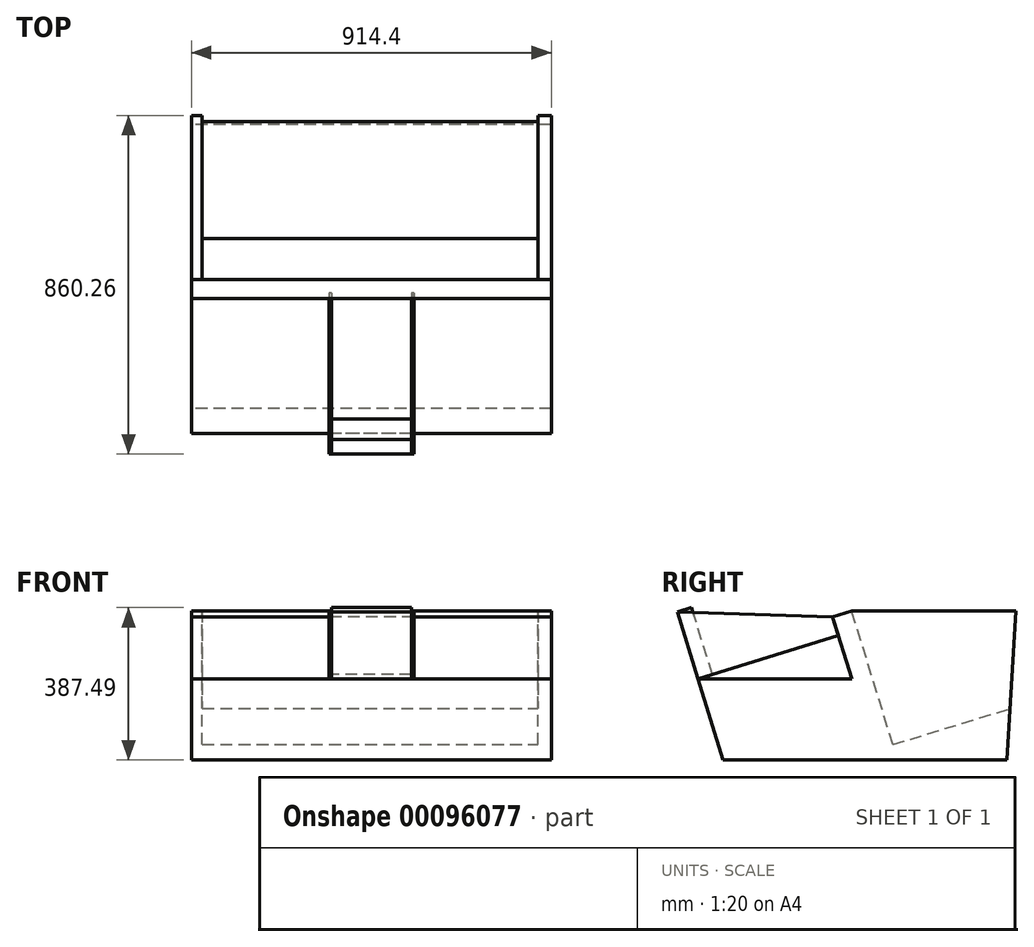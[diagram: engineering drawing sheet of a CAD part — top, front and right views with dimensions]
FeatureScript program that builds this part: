
annotation { "Feature Type Name" : "Feature", "Feature Type Description" : "" }
export const myFeature = defineFeature(function(context is Context, id is Id, definition is map)
    precondition{}
    {
        {
            var Q0;
            Q0=qCreatedBy(makeId("Right.planeOp"),FACE);
            var sketch = newSketch(context, id + "F0", { "sketchPlane" : qUnion([Q0])});
            skLineSegment(sketch, "E0", {"start": v(-51.02, 165.8) * mm, "end": v(61.03, -198.34) * mm});
            skLineSegment(sketch, "E1", {"start": v(-2.47, 8.01) * mm, "end": v(-393.28, 8.01) * mm});
            skLineSegment(sketch, "E2", {"start": v(-393.28, 8.01) * mm, "end": v(-329.78, -198.34) * mm});
            skLineSegment(sketch, "E3", {"start": v(-329.78, -198.34) * mm, "end": v(391.76, -198.34) * mm});
            skLineSegment(sketch, "E4", {"start": v(-51.02, 165.8) * mm, "end": v(-2.47, 180.75) * mm});
            skLineSegment(sketch, "E5", {"start": v(-2.47, 180.75) * mm, "end": v(414.68, 180.75) * mm});
            skLineSegment(sketch, "E6", {"start": v(-2.47, 180.75) * mm, "end": v(114.19, -198.34) * mm});
            skLineSegment(sketch, "E7", {"start": v(414.68, 180.75) * mm, "end": v(391.76, -198.34) * mm});
            skSolve(sketch);
        }
        {
            var Q0;
            {var subQ0=sQuery(id+"F0.wireOp",EDGE,"E4");Q0=makeQuery(id+"F0.imprint","IMPRINT",FACE,{"disambiguationData":[TD([[makeQuery(id+"F0.imprint","IMPRINT",EDGE,{"derivedFrom":subQ0}),-1.0]])]});}
            var Q1;
            {var subQ3=sQuery(id+"F0.wireOp",EDGE,"E1");Q1=makeQuery(id+"F0.imprint","IMPRINT",FACE,{"disambiguationData":[TD([[makeQuery(id+"F0.imprint","IMPRINT",EDGE,{"derivedFrom":subQ3}),1.0]])]});}
            var Q2;
            Q2=makeQuery(id+"F0.imprint","IMPRINT",FACE,{"disambiguationData":[TD([[makeQuery(id+"F0.imprint","IMPRINT",EDGE,{"derivedFrom":sQuery(id+"F0.wireOp",EDGE,"E5")}),-1.0]])]});
            extrude(context, id + "F1", {"entities" : qUnion([Q0, Q1, Q2]), "endBound" : BoundingType.SYMMETRIC, "depth" : 914.4 * mm});
        }
        {
            var Q0;
            Q0=makeQuery(id+"F1.opExtrude","SWEPT_FACE",FACE,{"disambiguationData":[OSD([sQuery(id+"F0.wireOp",EDGE,"E4")])]});
            cPlane(context, id + "F2", {"entities" : qUnion([Q0]), "cplaneType" : CPlaneType.OFFSET, "offset" : 0 * mm, "width" : 152.4 * mm, "height" : 152.4 * mm});
        }
        {
            var Q0;
            Q0=qCreatedBy(id+"F2.planeOp",FACE);
            var sketch = newSketch(context, id + "F3", { "sketchPlane" : qUnion([Q0])});
            skLineSegment(sketch, "E8.bottom", {"start": v(-429.68, 50.78) * mm, "end": v(423.77, 50.78) * mm});
            skLineSegment(sketch, "E8.top", {"start": v(-429.68, 469.65) * mm, "end": v(423.77, 469.65) * mm});
            skLineSegment(sketch, "E8.left", {"start": v(-429.68, 50.78) * mm, "end": v(-429.68, 469.65) * mm});
            skLineSegment(sketch, "E8.right", {"start": v(423.77, 50.78) * mm, "end": v(423.77, 469.65) * mm});
            skSolve(sketch);
        }
        {
            var Q0;
            Q0=makeQuery(id+"F3.imprint","IMPRINT",FACE,{"disambiguationData":[TD([[makeQuery(id+"F3.imprint","IMPRINT",EDGE,{"derivedFrom":sQuery(id+"F3.wireOp",EDGE,"E8.bottom")}),1.0]])]});
            extrude(context, id + "F4", {"entities" : qUnion([Q0]), "operationType" : NewBodyOperationType.REMOVE, "oppositeDirection" : true, "depth" : 355.6 * mm});
        }
        {
            var Q0;
            Q0=makeQuery(id+"F1.opExtrude","SWEPT_FACE",FACE,{"disambiguationData":[OSD([sQuery(id+"F0.wireOp",EDGE,"E2")])]});
            var sketch = newSketch(context, id + "F5", { "sketchPlane" : qUnion([Q0])});
            skLineSegment(sketch, "E9.bottom", {"start": v(-101.6, 123.33) * mm, "end": v(101.6, 123.33) * mm});
            skLineSegment(sketch, "E9.top", {"start": v(-101.6, 301.13) * mm, "end": v(101.6, 301.13) * mm});
            skLineSegment(sketch, "E9.left", {"start": v(-101.6, 123.33) * mm, "end": v(-101.6, 301.13) * mm});
            skLineSegment(sketch, "E9.right", {"start": v(101.6, 123.33) * mm, "end": v(101.6, 301.13) * mm});
            skLineSegment(sketch, "E10.bottom", {"start": v(101.6, 301.13) * mm, "end": v(107.95, 301.13) * mm});
            skLineSegment(sketch, "E10.top", {"start": v(101.6, 123.33) * mm, "end": v(107.95, 123.33) * mm});
            skLineSegment(sketch, "E10.left", {"start": v(101.6, 301.13) * mm, "end": v(101.6, 123.33) * mm});
            skLineSegment(sketch, "E10.right", {"start": v(107.95, 301.13) * mm, "end": v(107.95, 123.33) * mm});
            skLineSegment(sketch, "E11.bottom", {"start": v(-101.6, 123.33) * mm, "end": v(-107.95, 123.33) * mm});
            skLineSegment(sketch, "E11.top", {"start": v(-101.6, 301.13) * mm, "end": v(-107.95, 301.13) * mm});
            skLineSegment(sketch, "E11.right", {"start": v(-107.95, 123.33) * mm, "end": v(-107.95, 301.13) * mm});
            skSolve(sketch);
        }
        {
            var Q0;
            Q0=makeQuery(id+"F5.imprint","IMPRINT",FACE,{"disambiguationData":[TD([[makeQuery(id+"F5.imprint","IMPRINT",EDGE,{"derivedFrom":sQuery(id+"F5.wireOp",EDGE,"E9.bottom")}),-1.0]])]});
            extrude(context, id + "F6", {"entities" : qUnion([Q0]), "oppositeDirection" : true, "depth" : 38.1 * mm});
        }
        {
            var Q0;
            Q0=qCreatedBy(makeId("Front.planeOp"),FACE);
            cPlane(context, id + "F7", {"entities" : qUnion([Q0]), "cplaneType" : CPlaneType.OFFSET, "offset" : 457.2 * mm, "width" : 152.4 * mm, "height" : 152.4 * mm});
        }
        {
            var Q0;
            Q0=qCreatedBy(id+"F7.planeOp",FACE);
            var sketch = newSketch(context, id + "F8", { "sketchPlane" : qUnion([Q0])});
            skLineSegment(sketch, "E12.bottom", {"start": v(101.6, 0) * mm, "end": v(107.95, 0) * mm});
            skLineSegment(sketch, "E12.top", {"start": v(101.6, 170.23) * mm, "end": v(107.95, 170.23) * mm});
            skLineSegment(sketch, "E12.left", {"start": v(101.6, 0) * mm, "end": v(101.6, 170.23) * mm});
            skLineSegment(sketch, "E12.right", {"start": v(107.95, 0) * mm, "end": v(107.95, 170.23) * mm});
            skLineSegment(sketch, "E13.bottom", {"start": v(-101.6, 8.01) * mm, "end": v(-107.95, 8.01) * mm});
            skLineSegment(sketch, "E13.top", {"start": v(-101.6, 178.24) * mm, "end": v(-107.95, 178.24) * mm});
            skLineSegment(sketch, "E13.left", {"start": v(-101.6, 8.01) * mm, "end": v(-101.6, 178.24) * mm});
            skLineSegment(sketch, "E13.right", {"start": v(-107.95, 8.01) * mm, "end": v(-107.95, 178.24) * mm});
            skSolve(sketch);
        }
        {
            var Q0;
            Q0=makeQuery(id+"F5.imprint","IMPRINT",FACE,{"disambiguationData":[TD([[makeQuery(id+"F5.imprint","IMPRINT",EDGE,{"derivedFrom":sQuery(id+"F5.wireOp",EDGE,"E10.bottom")}),-1.0]])]});
            var Q1;
            Q1=makeQuery(id+"F5.imprint","IMPRINT",FACE,{"disambiguationData":[TD([[makeQuery(id+"F5.imprint","IMPRINT",EDGE,{"derivedFrom":sQuery(id+"F5.wireOp",EDGE,"E11.bottom")}),-1.0]])]});
            extrude(context, id + "F9", {"entities" : qUnion([Q0, Q1]), "oppositeDirection" : true, "depth" : 373.38 * mm});
        }
        {
            var Q0;
            Q0=makeQuery(id+"F9.opExtrude","SWEPT_FACE",FACE,{"disambiguationData":[OSD([sQuery(id+"F5.wireOp",EDGE,"E10.right")])]});
            var sketch = newSketch(context, id + "F10", { "sketchPlane" : qUnion([Q0])});
            skLineSegment(sketch, "E14", {"start": v(-51.03, 165.8) * mm, "end": v(-445.58, 177.95) * mm});
            skLineSegment(sketch, "E15", {"start": v(-445.58, 177.95) * mm, "end": v(-88.71, 287.77) * mm});
            skLineSegment(sketch, "E16", {"start": v(-88.71, 287.77) * mm, "end": v(-51.03, 165.8) * mm});
            skSolve(sketch);
        }
        {
            var Q0;
            {var subQ0=sQuery(id+"F10.wireOp",EDGE,"E16");Q0=makeQuery(id+"F10.imprint","IMPRINT",FACE,{"disambiguationData":[TD([[makeQuery(id+"F10.imprint","IMPRINT",EDGE,{"derivedFrom":subQ0}),-1.0]])]});}
            var Q1;
            {var subQ0=sQuery(id+"F10.wireOp",EDGE,"E15");Q1=makeQuery(id+"F10.imprint","IMPRINT",FACE,{"disambiguationData":[TD([[makeQuery(id+"F10.imprint","IMPRINT",EDGE,{"derivedFrom":subQ0}),1.0]])]});}
            extrude(context, id + "F11", {"entities" : qUnion([Q0, Q1]), "operationType" : NewBodyOperationType.REMOVE, "oppositeDirection" : true, "depth" : 6.35 * mm});
        }
        {
            var Q0;
            Q0=makeQuery(id+"F9.opExtrude","SWEPT_FACE",FACE,{"disambiguationData":[OSD([sQuery(id+"F5.wireOp",EDGE,"E11.right")])]});
            var sketch = newSketch(context, id + "F12", { "sketchPlane" : qUnion([Q0])});
            skLineSegment(sketch, "E17", {"start": v(51.2, 165.88) * mm, "end": v(445.58, 177.95) * mm});
            skLineSegment(sketch, "E18", {"start": v(88.71, 287.77) * mm, "end": v(51.2, 165.88) * mm});
            skSolve(sketch);
        }
        {
            var Q0;
            Q0=makeQuery(id+"F12.imprint","IMPRINT",FACE,{"disambiguationData":[TD([[makeQuery(id+"F12.imprint","IMPRINT",EDGE,{"derivedFrom":sQuery(id+"F12.wireOp",EDGE,"E17")}),1.0]])]});
            extrude(context, id + "F13", {"entities" : qUnion([Q0]), "operationType" : NewBodyOperationType.REMOVE, "oppositeDirection" : true, "depth" : 6.35 * mm});
        }
    });
